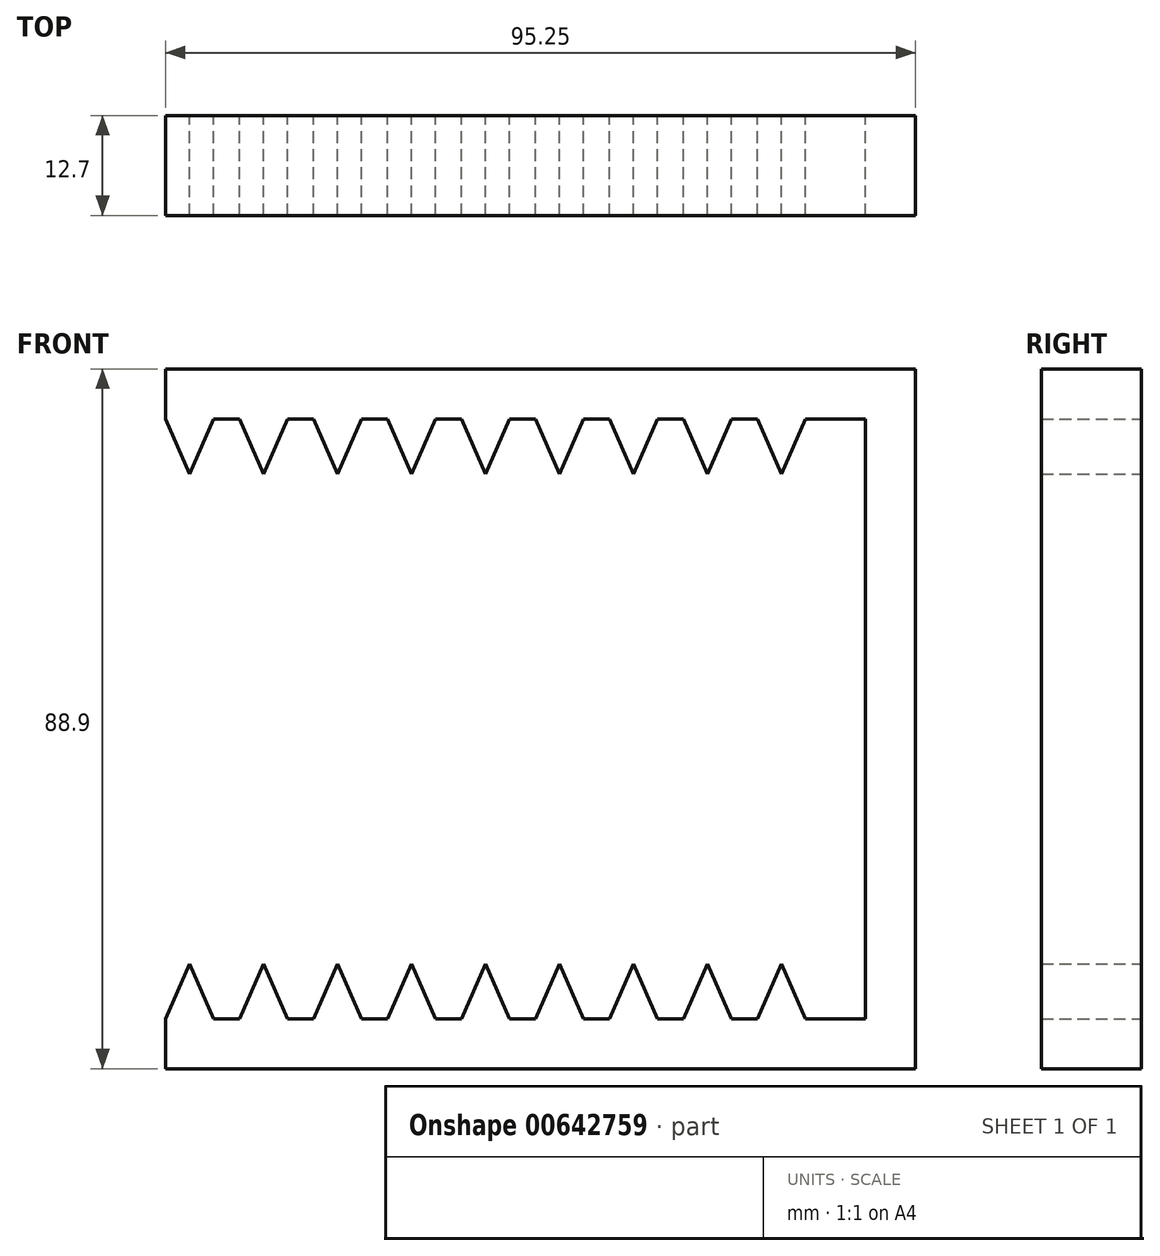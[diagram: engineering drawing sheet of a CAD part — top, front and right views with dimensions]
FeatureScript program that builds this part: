
annotation { "Feature Type Name" : "Feature", "Feature Type Description" : "" }
export const myFeature = defineFeature(function(context is Context, id is Id, definition is map)
    precondition{}
    {
        {
            var Q0;
            Q0=qCreatedBy(makeId("Front.planeOp"),FACE);
            var sketch = newSketch(context, id + "F0", { "sketchPlane" : qUnion([Q0])});
            skLineSegment(sketch, "E0.bottom", {"start": v(36.1, 44.45) * mm, "end": v(42.45, 44.45) * mm});
            skLineSegment(sketch, "E0.top", {"start": v(36.1, -44.45) * mm, "end": v(42.45, -44.45) * mm});
            skLineSegment(sketch, "E0.left", {"start": v(36.1, 44.45) * mm, "end": v(36.1, -44.45) * mm});
            skLineSegment(sketch, "E0.right", {"start": v(42.45, 44.45) * mm, "end": v(42.45, -44.45) * mm});
            skPoint(sketch, "E0.middle", {"position": v(39.27, 0) * mm});
            skLineSegment(sketch, "E1.bottom", {"start": v(36.1, 44.45) * mm, "end": v(-52.8, 44.45) * mm});
            skLineSegment(sketch, "E1.top", {"start": v(36.1, 38.1) * mm, "end": v(-52.8, 38.1) * mm});
            skLineSegment(sketch, "E1.left", {"start": v(36.1, 44.45) * mm, "end": v(36.1, 38.1) * mm});
            skLineSegment(sketch, "E1.right", {"start": v(-52.8, 44.45) * mm, "end": v(-52.8, 38.1) * mm});
            skLineSegment(sketch, "E2.MirrorCS", {"start": v(36.1, -44.45) * mm, "end": v(-52.8, -44.45) * mm});
            skLineSegment(sketch, "E3.MirrorCS", {"start": v(36.1, -38.1) * mm, "end": v(-52.8, -38.1) * mm});
            skLineSegment(sketch, "E4.MirrorCS", {"start": v(-52.8, -44.45) * mm, "end": v(-52.8, -38.1) * mm});
            skLineSegment(sketch, "E5.MirrorCS", {"start": v(36.1, -44.45) * mm, "end": v(36.1, -38.1) * mm});
            skLineSegment(sketch, "E6", {"start": v(-49.75, 38.1) * mm, "end": v(-49.75, 31.12) * mm, "construction": true});
            skLineSegment(sketch, "E7", {"start": v(-49.75, 31.12) * mm, "end": v(-52.8, 38.1) * mm});
            skLineSegment(sketch, "E8.MirrorCS", {"start": v(-49.75, 31.12) * mm, "end": v(-46.7, 38.1) * mm});
            skLineSegment(sketch, "E9.1.0.0", {"start": v(-40.35, 31.12) * mm, "end": v(-43.4, 38.1) * mm});
            skLineSegment(sketch, "E9.1.0.1", {"start": v(-40.35, 31.12) * mm, "end": v(-37.3, 38.1) * mm});
            skLineSegment(sketch, "E9.2.0.0", {"start": v(-30.95, 31.12) * mm, "end": v(-34, 38.1) * mm});
            skLineSegment(sketch, "E9.2.0.1", {"start": v(-30.95, 31.12) * mm, "end": v(-27.9, 38.1) * mm});
            skLineSegment(sketch, "E9.3.0.0", {"start": v(-21.56, 31.12) * mm, "end": v(-24.6, 38.1) * mm});
            skLineSegment(sketch, "E9.3.0.1", {"start": v(-21.56, 31.12) * mm, "end": v(-18.5, 38.1) * mm});
            skLineSegment(sketch, "E9.4.0.0", {"start": v(-12.16, 31.12) * mm, "end": v(-15.21, 38.1) * mm});
            skLineSegment(sketch, "E9.4.0.1", {"start": v(-12.16, 31.12) * mm, "end": v(-9.1, 38.1) * mm});
            skLineSegment(sketch, "E9.5.0.0", {"start": v(-2.76, 31.12) * mm, "end": v(-5.81, 38.1) * mm});
            skLineSegment(sketch, "E9.5.0.1", {"start": v(-2.76, 31.12) * mm, "end": v(0.3, 38.1) * mm});
            skLineSegment(sketch, "E9.6.0.0", {"start": v(6.64, 31.12) * mm, "end": v(3.58, 38.1) * mm});
            skLineSegment(sketch, "E9.6.0.1", {"start": v(6.64, 31.12) * mm, "end": v(9.7, 38.1) * mm});
            skLineSegment(sketch, "E9.7.0.0", {"start": v(16.04, 31.12) * mm, "end": v(12.98, 38.1) * mm});
            skLineSegment(sketch, "E9.7.0.1", {"start": v(16.04, 31.12) * mm, "end": v(19.09, 38.1) * mm});
            skLineSegment(sketch, "E9.8.0.0", {"start": v(25.43, 31.12) * mm, "end": v(22.38, 38.1) * mm});
            skLineSegment(sketch, "E9.8.0.1", {"start": v(25.43, 31.12) * mm, "end": v(28.49, 38.1) * mm});
            skLineSegment(sketch, "E9.direction1", {"start": v(-49.75, 31.12) * mm, "end": v(-40.35, 31.12) * mm, "construction": true});
            skLineSegment(sketch, "E10.MirrorCS", {"start": v(-49.75, -31.12) * mm, "end": v(-52.8, -38.1) * mm});
            skLineSegment(sketch, "E11.MirrorCS", {"start": v(-49.75, -31.12) * mm, "end": v(-46.7, -38.1) * mm});
            skLineSegment(sketch, "E12.MirrorCS", {"start": v(-40.35, -31.12) * mm, "end": v(-43.4, -38.1) * mm});
            skLineSegment(sketch, "E13.MirrorCS", {"start": v(-40.35, -31.12) * mm, "end": v(-37.3, -38.1) * mm});
            skLineSegment(sketch, "E14.MirrorCS", {"start": v(-30.95, -31.12) * mm, "end": v(-27.9, -38.1) * mm});
            skLineSegment(sketch, "E15.MirrorCS", {"start": v(-21.56, -31.12) * mm, "end": v(-24.6, -38.1) * mm});
            skLineSegment(sketch, "E16.MirrorCS", {"start": v(-21.56, -31.12) * mm, "end": v(-18.5, -38.1) * mm});
            skLineSegment(sketch, "E17.MirrorCS", {"start": v(-12.16, -31.12) * mm, "end": v(-15.21, -38.1) * mm});
            skLineSegment(sketch, "E18.MirrorCS", {"start": v(-12.16, -31.12) * mm, "end": v(-9.1, -38.1) * mm});
            skLineSegment(sketch, "E19.MirrorCS", {"start": v(-2.76, -31.12) * mm, "end": v(-5.81, -38.1) * mm});
            skLineSegment(sketch, "E20.MirrorCS", {"start": v(-2.76, -31.12) * mm, "end": v(0.3, -38.1) * mm});
            skLineSegment(sketch, "E21.MirrorCS", {"start": v(6.64, -31.12) * mm, "end": v(3.58, -38.1) * mm});
            skLineSegment(sketch, "E22.MirrorCS", {"start": v(6.64, -31.12) * mm, "end": v(9.7, -38.1) * mm});
            skLineSegment(sketch, "E23.MirrorCS", {"start": v(16.04, -31.12) * mm, "end": v(12.98, -38.1) * mm});
            skLineSegment(sketch, "E24.MirrorCS", {"start": v(16.04, -31.12) * mm, "end": v(19.09, -38.1) * mm});
            skLineSegment(sketch, "E25.MirrorCS", {"start": v(25.43, -31.12) * mm, "end": v(22.38, -38.1) * mm});
            skLineSegment(sketch, "E26.MirrorCS", {"start": v(25.43, -31.12) * mm, "end": v(28.49, -38.1) * mm});
            skLineSegment(sketch, "E27.MirrorCS", {"start": v(-30.95, -31.12) * mm, "end": v(-34, -38.1) * mm});
            skSolve(sketch);
        }
        {
            var Q0;
            Q0=makeQuery(id+"F0.imprint","IMPRINT",FACE,{"disambiguationData":[TD([[makeQuery(id+"F0.imprint","IMPRINT",EDGE,{"derivedFrom":sQuery(id+"F0.wireOp",EDGE,"E2.MirrorCS")}),-1.0]])]});
            var Q1;
            {var subQ0=sQuery(id+"F0.wireOp",EDGE,"E15.MirrorCS");Q1=makeQuery(id+"F0.imprint","IMPRINT",FACE,{"disambiguationData":[TD([[makeQuery(id+"F0.imprint","IMPRINT",EDGE,{"derivedFrom":subQ0}),1.0]])]});}
            var Q2;
            {var subQ0=sQuery(id+"F0.wireOp",EDGE,"E25.MirrorCS");Q2=makeQuery(id+"F0.imprint","IMPRINT",FACE,{"disambiguationData":[TD([[makeQuery(id+"F0.imprint","IMPRINT",EDGE,{"derivedFrom":subQ0}),1.0]])]});}
            var Q3;
            Q3=makeQuery(id+"F0.imprint","IMPRINT",FACE,{"disambiguationData":[TD([[makeQuery(id+"F0.imprint","IMPRINT",EDGE,{"derivedFrom":sQuery(id+"F0.wireOp",EDGE,"E0.bottom")}),-1.0]])]});
            var Q4;
            {var subQ0=sQuery(id+"F0.wireOp",EDGE,"E14.MirrorCS");Q4=makeQuery(id+"F0.imprint","IMPRINT",FACE,{"disambiguationData":[TD([[makeQuery(id+"F0.imprint","IMPRINT",EDGE,{"derivedFrom":subQ0}),-1.0]])]});}
            var Q5;
            Q5=makeQuery(id+"F0.imprint","IMPRINT",FACE,{"disambiguationData":[TD([[makeQuery(id+"F0.imprint","IMPRINT",EDGE,{"derivedFrom":sQuery(id+"F0.wireOp",EDGE,"E1.bottom")}),1.0]])]});
            var Q6;
            {var subQ0=sQuery(id+"F0.wireOp",EDGE,"E12.MirrorCS");Q6=makeQuery(id+"F0.imprint","IMPRINT",FACE,{"disambiguationData":[TD([[makeQuery(id+"F0.imprint","IMPRINT",EDGE,{"derivedFrom":subQ0}),1.0]])]});}
            var Q7;
            {var subQ0=sQuery(id+"F0.wireOp",EDGE,"E19.MirrorCS");Q7=makeQuery(id+"F0.imprint","IMPRINT",FACE,{"disambiguationData":[TD([[makeQuery(id+"F0.imprint","IMPRINT",EDGE,{"derivedFrom":subQ0}),1.0]])]});}
            var Q8;
            {var subQ0=sQuery(id+"F0.wireOp",EDGE,"E9.1.0.0");Q8=makeQuery(id+"F0.imprint","IMPRINT",FACE,{"disambiguationData":[TD([[makeQuery(id+"F0.imprint","IMPRINT",EDGE,{"derivedFrom":subQ0}),-1.0]])]});}
            var Q9;
            {var subQ0=sQuery(id+"F0.wireOp",EDGE,"E9.4.0.0");Q9=makeQuery(id+"F0.imprint","IMPRINT",FACE,{"disambiguationData":[TD([[makeQuery(id+"F0.imprint","IMPRINT",EDGE,{"derivedFrom":subQ0}),-1.0]])]});}
            var Q10;
            {var subQ0=sQuery(id+"F0.wireOp",EDGE,"E9.2.0.0");Q10=makeQuery(id+"F0.imprint","IMPRINT",FACE,{"disambiguationData":[TD([[makeQuery(id+"F0.imprint","IMPRINT",EDGE,{"derivedFrom":subQ0}),-1.0]])]});}
            var Q11;
            {var subQ0=sQuery(id+"F0.wireOp",EDGE,"E21.MirrorCS");Q11=makeQuery(id+"F0.imprint","IMPRINT",FACE,{"disambiguationData":[TD([[makeQuery(id+"F0.imprint","IMPRINT",EDGE,{"derivedFrom":subQ0}),1.0]])]});}
            var Q12;
            {var subQ0=sQuery(id+"F0.wireOp",EDGE,"E9.7.0.0");Q12=makeQuery(id+"F0.imprint","IMPRINT",FACE,{"disambiguationData":[TD([[makeQuery(id+"F0.imprint","IMPRINT",EDGE,{"derivedFrom":subQ0}),-1.0]])]});}
            var Q13;
            {var subQ0=sQuery(id+"F0.wireOp",EDGE,"E7");Q13=makeQuery(id+"F0.imprint","IMPRINT",FACE,{"disambiguationData":[TD([[makeQuery(id+"F0.imprint","IMPRINT",EDGE,{"derivedFrom":subQ0}),-1.0]])]});}
            var Q14;
            {var subQ0=sQuery(id+"F0.wireOp",EDGE,"E9.6.0.0");Q14=makeQuery(id+"F0.imprint","IMPRINT",FACE,{"disambiguationData":[TD([[makeQuery(id+"F0.imprint","IMPRINT",EDGE,{"derivedFrom":subQ0}),-1.0]])]});}
            var Q15;
            {var subQ0=sQuery(id+"F0.wireOp",EDGE,"E9.8.0.0");Q15=makeQuery(id+"F0.imprint","IMPRINT",FACE,{"disambiguationData":[TD([[makeQuery(id+"F0.imprint","IMPRINT",EDGE,{"derivedFrom":subQ0}),-1.0]])]});}
            var Q16;
            {var subQ0=sQuery(id+"F0.wireOp",EDGE,"E23.MirrorCS");Q16=makeQuery(id+"F0.imprint","IMPRINT",FACE,{"disambiguationData":[TD([[makeQuery(id+"F0.imprint","IMPRINT",EDGE,{"derivedFrom":subQ0}),1.0]])]});}
            var Q17;
            {var subQ0=sQuery(id+"F0.wireOp",EDGE,"E9.5.0.0");Q17=makeQuery(id+"F0.imprint","IMPRINT",FACE,{"disambiguationData":[TD([[makeQuery(id+"F0.imprint","IMPRINT",EDGE,{"derivedFrom":subQ0}),-1.0]])]});}
            var Q18;
            {var subQ0=sQuery(id+"F0.wireOp",EDGE,"E9.3.0.0");Q18=makeQuery(id+"F0.imprint","IMPRINT",FACE,{"disambiguationData":[TD([[makeQuery(id+"F0.imprint","IMPRINT",EDGE,{"derivedFrom":subQ0}),-1.0]])]});}
            var Q19;
            {var subQ0=sQuery(id+"F0.wireOp",EDGE,"E10.MirrorCS");Q19=makeQuery(id+"F0.imprint","IMPRINT",FACE,{"disambiguationData":[TD([[makeQuery(id+"F0.imprint","IMPRINT",EDGE,{"derivedFrom":subQ0}),1.0]])]});}
            var Q20;
            {var subQ0=sQuery(id+"F0.wireOp",EDGE,"E17.MirrorCS");Q20=makeQuery(id+"F0.imprint","IMPRINT",FACE,{"disambiguationData":[TD([[makeQuery(id+"F0.imprint","IMPRINT",EDGE,{"derivedFrom":subQ0}),1.0]])]});}
            extrude(context, id + "F1", {"entities" : qUnion([Q0, Q1, Q2, Q3, Q4, Q5, Q6, Q7, Q8, Q9, Q10, Q11, Q12, Q13, Q14, Q15, Q16, Q17, Q18, Q19, Q20]), "depth" : 12.7 * mm, "offsetDistance" : 25.4 * mm});
        }
    });
